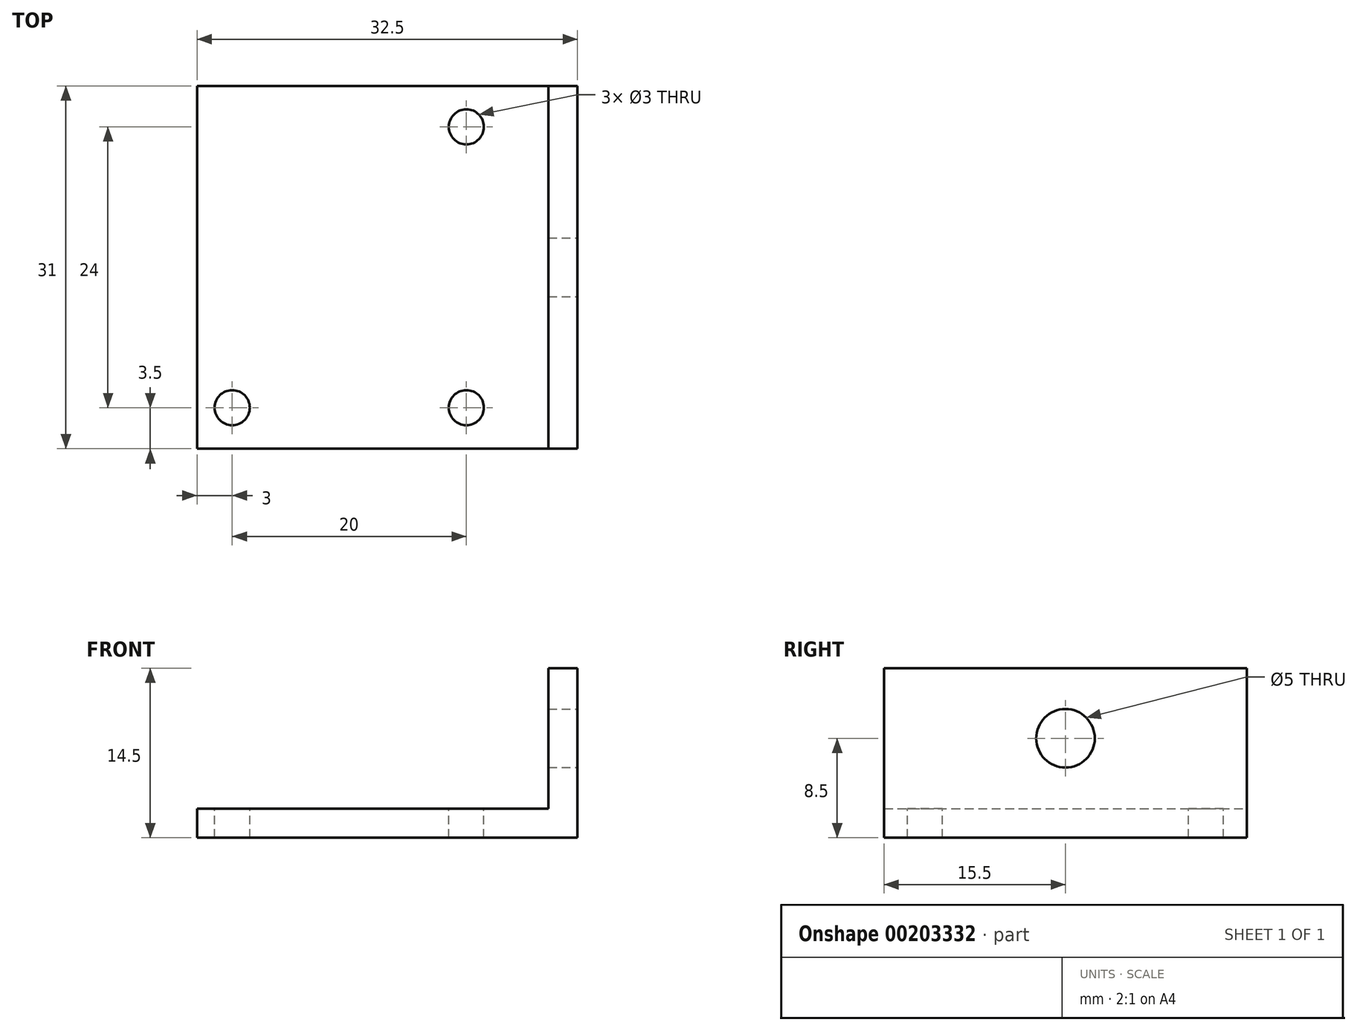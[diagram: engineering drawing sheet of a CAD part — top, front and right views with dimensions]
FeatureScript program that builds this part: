
annotation { "Feature Type Name" : "Feature", "Feature Type Description" : "" }
export const myFeature = defineFeature(function(context is Context, id is Id, definition is map)
    precondition{}
    {
        {
            var Q0;
            Q0=qCreatedBy(makeId("Top.planeOp"),FACE);
            var sketch = newSketch(context, id + "F0", { "sketchPlane" : qUnion([Q0])});
            skLineSegment(sketch, "E0.bottom", {"start": v(15, -15.5) * mm, "end": v(-15, -15.5) * mm});
            skLineSegment(sketch, "E0.top", {"start": v(15, 15.5) * mm, "end": v(-15, 15.5) * mm});
            skLineSegment(sketch, "E0.left", {"start": v(15, -15.5) * mm, "end": v(15, 15.5) * mm});
            skLineSegment(sketch, "E0.right", {"start": v(-15, -15.5) * mm, "end": v(-15, 15.5) * mm});
            skPoint(sketch, "E0.middle", {"position": v(0, 0) * mm});
            skSolve(sketch);
        }
        {
            var Q0;
            Q0 = qSketchRegion(id + "F0", true);
            extrude(context, id + "F1", {"entities" : qUnion([Q0]), "depth" : 2.5 * mm});
        }
        {
            var Q0;
            Q0=makeQuery(id+"F1.opExtrude","CAP_FACE",FACE,{"disambiguationData":[OSD([sQuery(id+"F0.wireOp",EDGE,"E0.bottom"),sQuery(id+"F0.wireOp",EDGE,"E0.top"),sQuery(id+"F0.wireOp",EDGE,"E0.left"),sQuery(id+"F0.wireOp",EDGE,"E0.right")])],"isStart":false});
            var sketch = newSketch(context, id + "F2", { "sketchPlane" : qUnion([Q0])});
            skLineSegment(sketch, "E1", {"start": v(-15, 0) * mm, "end": v(15, 0) * mm, "construction": true});
            skLineSegment(sketch, "E2", {"start": v(-15, -12) * mm, "end": v(15, -12) * mm, "construction": true});
            skCircle(sketch, "E3.MirrorC", {"center": v(-12, -12) * mm, "radius": 1.5 * mm});
            skLineSegment(sketch, "E4", {"start": v(-2, 15.5) * mm, "end": v(-2, -15.5) * mm, "construction": true});
            skCircle(sketch, "E5.MirrorC", {"center": v(8, -12) * mm, "radius": 1.5 * mm});
            skCircle(sketch, "E6.MirrorC", {"center": v(8, 12) * mm, "radius": 1.5 * mm});
            skSolve(sketch);
        }
        {
            var Q0;
            Q0 = qSketchRegion(id + "F2", true);
            extrude(context, id + "F3", {"entities" : qUnion([Q0]), "operationType" : NewBodyOperationType.REMOVE, "endBound" : BoundingType.THROUGH_ALL, "oppositeDirection" : true, "depth" : 25 * mm});
        }
        {
            var Q0;
            Q0=makeQuery(id+"F1.opExtrude","SWEPT_FACE",FACE,{"disambiguationData":[OSD([sQuery(id+"F0.wireOp",EDGE,"E0.left")])]});
            var sketch = newSketch(context, id + "F4", { "sketchPlane" : qUnion([Q0])});
            skLineSegment(sketch, "E7.bottom", {"start": v(-15.5, 0) * mm, "end": v(15.5, 0) * mm});
            skLineSegment(sketch, "E7.top", {"start": v(-15.5, 14.5) * mm, "end": v(15.5, 14.5) * mm});
            skLineSegment(sketch, "E7.left", {"start": v(-15.5, 0) * mm, "end": v(-15.5, 14.5) * mm});
            skLineSegment(sketch, "E7.right", {"start": v(15.5, 0) * mm, "end": v(15.5, 14.5) * mm});
            skSolve(sketch);
        }
        {
            var Q0;
            Q0 = qSketchRegion(id + "F4", true);
            extrude(context, id + "F5", {"entities" : qUnion([Q0]), "operationType" : NewBodyOperationType.ADD, "depth" : 2.5 * mm});
        }
        {
            var Q0;
            Q0=makeQuery(id+"F5.opExtrude","CAP_FACE",FACE,{"disambiguationData":[OSD([sQuery(id+"F4.wireOp",EDGE,"E7.bottom"),sQuery(id+"F4.wireOp",EDGE,"E7.top"),sQuery(id+"F4.wireOp",EDGE,"E7.left"),sQuery(id+"F4.wireOp",EDGE,"E7.right")])],"isStart":false});
            var sketch = newSketch(context, id + "F6", { "sketchPlane" : qUnion([Q0])});
            skLineSegment(sketch, "E8", {"start": v(0, 14.5) * mm, "end": v(0, 0) * mm, "construction": true});
            skLineSegment(sketch, "E9", {"start": v(-15.5, 8.5) * mm, "end": v(15.5, 8.5) * mm, "construction": true});
            skCircle(sketch, "E10", {"center": v(0, 8.5) * mm, "radius": 2.5 * mm});
            skSolve(sketch);
        }
        {
            var Q0;
            Q0 = qSketchRegion(id + "F6", true);
            extrude(context, id + "F7", {"entities" : qUnion([Q0]), "operationType" : NewBodyOperationType.REMOVE, "endBound" : BoundingType.THROUGH_ALL, "oppositeDirection" : true, "depth" : 10 * mm});
        }
    });
